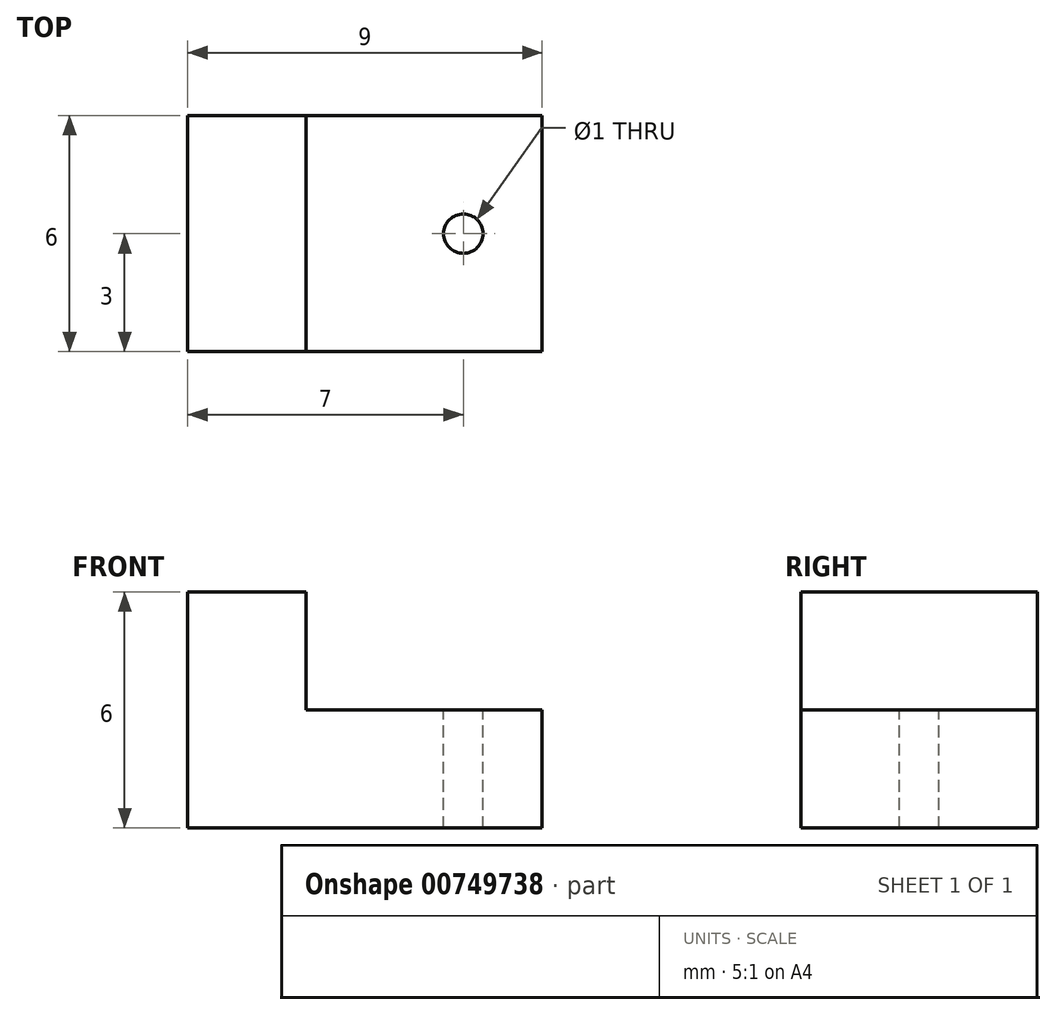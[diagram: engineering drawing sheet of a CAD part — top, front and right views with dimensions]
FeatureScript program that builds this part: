
annotation { "Feature Type Name" : "Feature", "Feature Type Description" : "" }
export const myFeature = defineFeature(function(context is Context, id is Id, definition is map)
    precondition{}
    {
        {
            var Q0;
            Q0=qCreatedBy(makeId("Front.planeOp"),FACE);
            var sketch = newSketch(context, id + "F0", { "sketchPlane" : qUnion([Q0])});
            skLineSegment(sketch, "E0", {"start": v(0, 0) * mm, "end": v(0, 6) * mm});
            skLineSegment(sketch, "E1", {"start": v(0, 6) * mm, "end": v(3, 6) * mm});
            skLineSegment(sketch, "E2", {"start": v(3, 6) * mm, "end": v(3, 3) * mm});
            skLineSegment(sketch, "E3", {"start": v(3, 3) * mm, "end": v(9, 3) * mm});
            skLineSegment(sketch, "E4", {"start": v(9, 3) * mm, "end": v(9, 0) * mm});
            skLineSegment(sketch, "E5", {"start": v(9, 0) * mm, "end": v(0, 0) * mm});
            skSolve(sketch);
        }
        {
            var Q0;
            Q0=makeQuery(id+"F0.imprint","IMPRINT",FACE,{"disambiguationData":[TD([[makeQuery(id+"F0.imprint","IMPRINT",EDGE,{"derivedFrom":sQuery(id+"F0.wireOp",EDGE,"E0")}),-1.0]])]});
            extrude(context, id + "F1", {"entities" : qUnion([Q0]), "depth" : 6 * mm, "offsetDistance" : 25 * mm});
        }
        {
            var Q0;
            Q0=makeQuery(id+"F1.opExtrude","SWEPT_FACE",FACE,{"disambiguationData":[OSD([sQuery(id+"F0.wireOp",EDGE,"E3")])]});
            var sketch = newSketch(context, id + "F2", { "sketchPlane" : qUnion([Q0])});
            skCircle(sketch, "E6", {"center": v(7, -3) * mm, "radius": 0.5 * mm});
            skSolve(sketch);
        }
        {
            var Q0;
            Q0=makeQuery(id+"F2.imprint","IMPRINT",FACE,{"disambiguationData":[TD([[makeQuery(id+"F2.imprint","IMPRINT",EDGE,{"derivedFrom":sQuery(id+"F2.wireOp",EDGE,"E6")}),1.0]])]});
            extrude(context, id + "F3", {"entities" : qUnion([Q0]), "operationType" : NewBodyOperationType.REMOVE, "endBound" : BoundingType.THROUGH_ALL, "oppositeDirection" : true, "depth" : 25 * mm, "offsetDistance" : 25 * mm});
        }
    });
